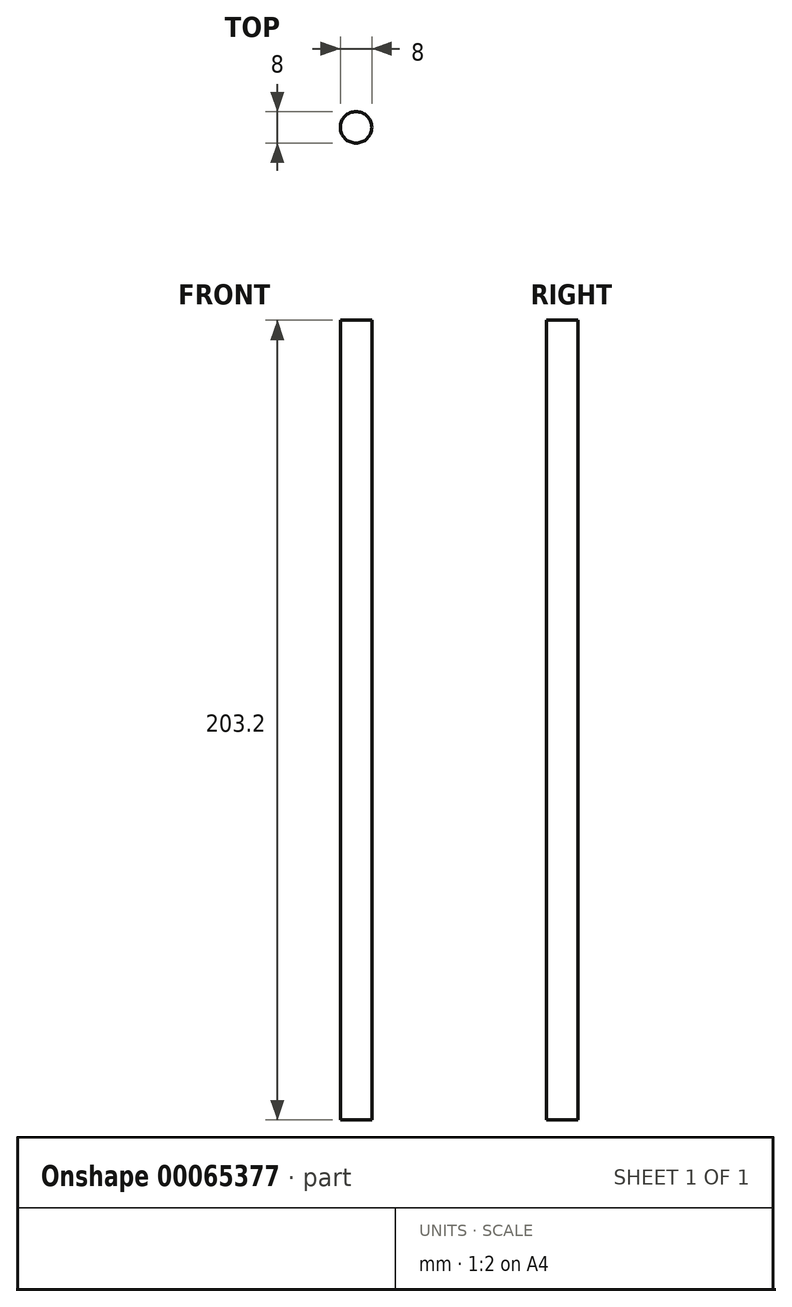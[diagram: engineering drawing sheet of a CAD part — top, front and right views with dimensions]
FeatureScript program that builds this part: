
annotation { "Feature Type Name" : "Feature", "Feature Type Description" : "" }
export const myFeature = defineFeature(function(context is Context, id is Id, definition is map)
    precondition{}
    {
        {
            var Q0;
            Q0=qCreatedBy(makeId("Top.planeOp"),FACE);
            var sketch = newSketch(context, id + "F0", { "sketchPlane" : qUnion([Q0])});
            skCircle(sketch, "E0", {"center": v(0, 0) * mm, "radius": 4 * mm});
            skSolve(sketch);
        }
        {
            var Q0;
            Q0=qSketchRegion(id+"F0",true);
            extrude(context, id + "F1", {"entities" : qUnion([Q0]), "depth" : 203.2 * mm});
        }
    });
